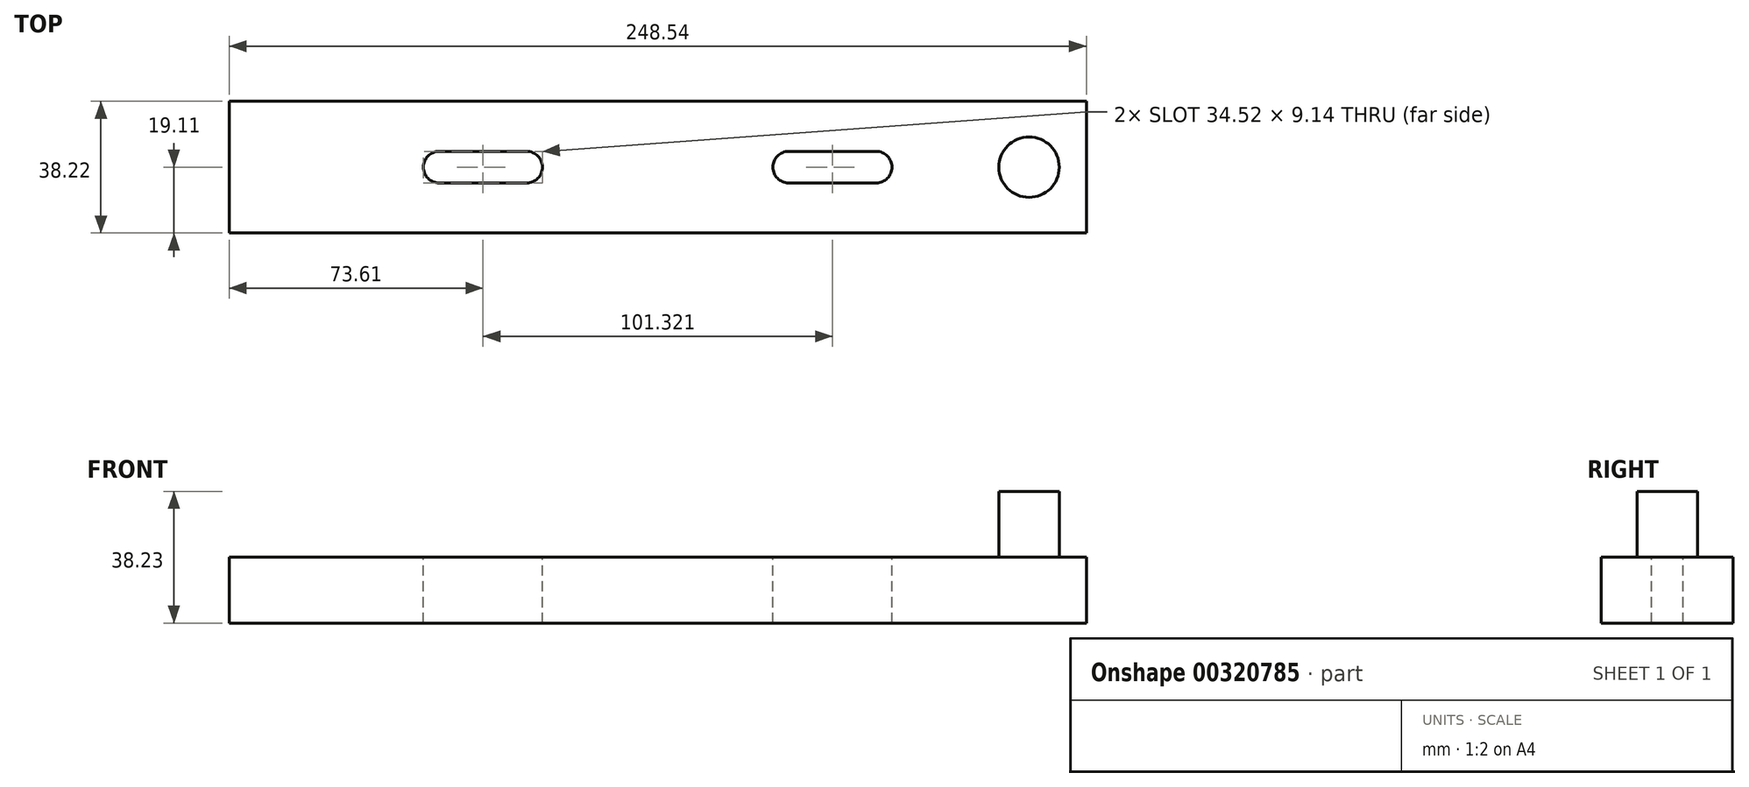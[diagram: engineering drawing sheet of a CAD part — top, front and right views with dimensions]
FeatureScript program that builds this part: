
annotation { "Feature Type Name" : "Feature", "Feature Type Description" : "" }
export const myFeature = defineFeature(function(context is Context, id is Id, definition is map)
    precondition{}
    {
        {
            var Q0;
            Q0=qCreatedBy(makeId("Top.planeOp"),FACE);
            var sketch = newSketch(context, id + "F0", { "sketchPlane" : qUnion([Q0])});
            skLineSegment(sketch, "E0.bottom", {"start": v(-124.27, -19.11) * mm, "end": v(124.27, -19.11) * mm});
            skLineSegment(sketch, "E0.top", {"start": v(-124.27, 19.11) * mm, "end": v(124.27, 19.11) * mm});
            skLineSegment(sketch, "E0.left", {"start": v(-124.27, -19.11) * mm, "end": v(-124.27, 19.11) * mm});
            skLineSegment(sketch, "E0.right", {"start": v(124.27, -19.11) * mm, "end": v(124.27, 19.11) * mm});
            skPoint(sketch, "E0.middle", {"position": v(0, 0) * mm});
            skSolve(sketch);
        }
        {
            var Q0;
            Q0 = qSketchRegion(id + "F0", true);
            extrude(context, id + "F1", {"entities" : qUnion([Q0]), "depth" : 38.23 * mm});
        }
        {
            var Q0;
            Q0=makeQuery(id+"F1.opExtrude","CAP_FACE",FACE,{"disambiguationData":[OSD([sQuery(id+"F0.wireOp",EDGE,"E0.bottom"),sQuery(id+"F0.wireOp",EDGE,"E0.top"),sQuery(id+"F0.wireOp",EDGE,"E0.left"),sQuery(id+"F0.wireOp",EDGE,"E0.right")])],"isStart":false});
            var sketch = newSketch(context, id + "F2", { "sketchPlane" : qUnion([Q0])});
            skLineSegment(sketch, "E1", {"start": v(0, 19.11) * mm, "end": v(0, -19.11) * mm, "construction": true});
            skCircle(sketch, "E2", {"center": v(0, 0) * mm, "radius": 3.94 * mm});
            skCircle(sketch, "E3", {"center": v(-107.67, 0) * mm, "radius": 8.76 * mm});
            skArc(sketch, "E4", {"start": v(-63.35, 4.57) * mm, "mid": v(-67.92, 0) * mm, "end": v(-63.35, -4.57) * mm});
            skArc(sketch, "E5", {"start": v(-37.97, -4.57) * mm, "mid": v(-33.4, 0) * mm, "end": v(-37.97, 4.57) * mm});
            skLineSegment(sketch, "E6", {"start": v(-63.35, 4.57) * mm, "end": v(-37.97, 4.57) * mm});
            skLineSegment(sketch, "E7", {"start": v(-63.35, -4.57) * mm, "end": v(-37.97, -4.57) * mm});
            skArc(sketch, "E8.MirrorCS", {"start": v(37.97, -4.57) * mm, "mid": v(33.4, 0) * mm, "end": v(37.97, 4.57) * mm});
            skLineSegment(sketch, "E9.MirrorCS", {"start": v(63.35, -4.57) * mm, "end": v(37.97, -4.57) * mm});
            skLineSegment(sketch, "E10.MirrorCS", {"start": v(63.35, 4.57) * mm, "end": v(37.97, 4.57) * mm});
            skArc(sketch, "E11.MirrorCS", {"start": v(63.35, 4.57) * mm, "mid": v(67.92, 0) * mm, "end": v(63.35, -4.57) * mm});
            skCircle(sketch, "E12.MirrorC", {"center": v(107.67, 0) * mm, "radius": 8.76 * mm});
            skSolve(sketch);
        }
        {
            var Q0;
            Q0=makeQuery(id+"F2.imprint","IMPRINT",FACE,{"disambiguationData":[TD([[makeQuery(id+"F2.imprint","IMPRINT",EDGE,{"derivedFrom":sQuery(id+"F2.wireOp",EDGE,"E3")}),1.0]])]});
            var Q1;
            Q1=makeQuery(id+"F2.imprint","IMPRINT",FACE,{"disambiguationData":[TD([[makeQuery(id+"F2.imprint","IMPRINT",EDGE,{"derivedFrom":sQuery(id+"F2.wireOp",EDGE,"E2")}),1.0]])]});
            var Q2;
            Q2=makeQuery(id+"F2.imprint","IMPRINT",FACE,{"disambiguationData":[TD([[makeQuery(id+"F2.imprint","IMPRINT",EDGE,{"derivedFrom":sQuery(id+"F2.wireOp",EDGE,"E12.MirrorC")}),-1.0]])]});
            extrude(context, id + "F3", {"entities" : qUnion([Q0, Q1, Q2]), "operationType" : NewBodyOperationType.REMOVE, "oppositeDirection" : true, "depth" : 19.05 * mm});
        }
        {
            var Q0;
            Q0=makeQuery(id+"F1.opExtrude","CAP_FACE",FACE,{"disambiguationData":[OSD([sQuery(id+"F0.wireOp",EDGE,"E0.bottom"),sQuery(id+"F0.wireOp",EDGE,"E0.top"),sQuery(id+"F0.wireOp",EDGE,"E0.left"),sQuery(id+"F0.wireOp",EDGE,"E0.right")])],"isStart":false});
            var sketch = newSketch(context, id + "F4", { "sketchPlane" : qUnion([Q0])});
            skLineSegment(sketch, "E13", {"start": v(0, 26.45) * mm, "end": v(0, -26.45) * mm, "construction": true});
            skArc(sketch, "E14", {"start": v(-63.35, 4.57) * mm, "mid": v(-67.92, 0) * mm, "end": v(-63.35, -4.57) * mm});
            skArc(sketch, "E15", {"start": v(-37.97, -4.57) * mm, "mid": v(-33.4, 0) * mm, "end": v(-37.97, 4.57) * mm});
            skLineSegment(sketch, "E16", {"start": v(-63.35, 4.57) * mm, "end": v(-37.97, 4.57) * mm});
            skLineSegment(sketch, "E17", {"start": v(-63.35, -4.57) * mm, "end": v(-37.97, -4.57) * mm});
            skArc(sketch, "E18.MirrorCS", {"start": v(37.97, -4.57) * mm, "mid": v(33.4, 0) * mm, "end": v(37.97, 4.57) * mm});
            skLineSegment(sketch, "E19.MirrorCS", {"start": v(63.35, -4.57) * mm, "end": v(37.97, -4.57) * mm});
            skLineSegment(sketch, "E20.MirrorCS", {"start": v(63.35, 4.57) * mm, "end": v(37.97, 4.57) * mm});
            skArc(sketch, "E21.MirrorCS", {"start": v(63.35, 4.57) * mm, "mid": v(67.92, 0) * mm, "end": v(63.35, -4.57) * mm});
            skSolve(sketch);
        }
        {
            var Q0;
            Q0 = qSketchRegion(id + "F4", true);
            extrude(context, id + "F5", {"entities" : qUnion([Q0]), "operationType" : NewBodyOperationType.REMOVE, "endBound" : BoundingType.THROUGH_ALL, "oppositeDirection" : true, "depth" : 25.4 * mm});
        }
    });
